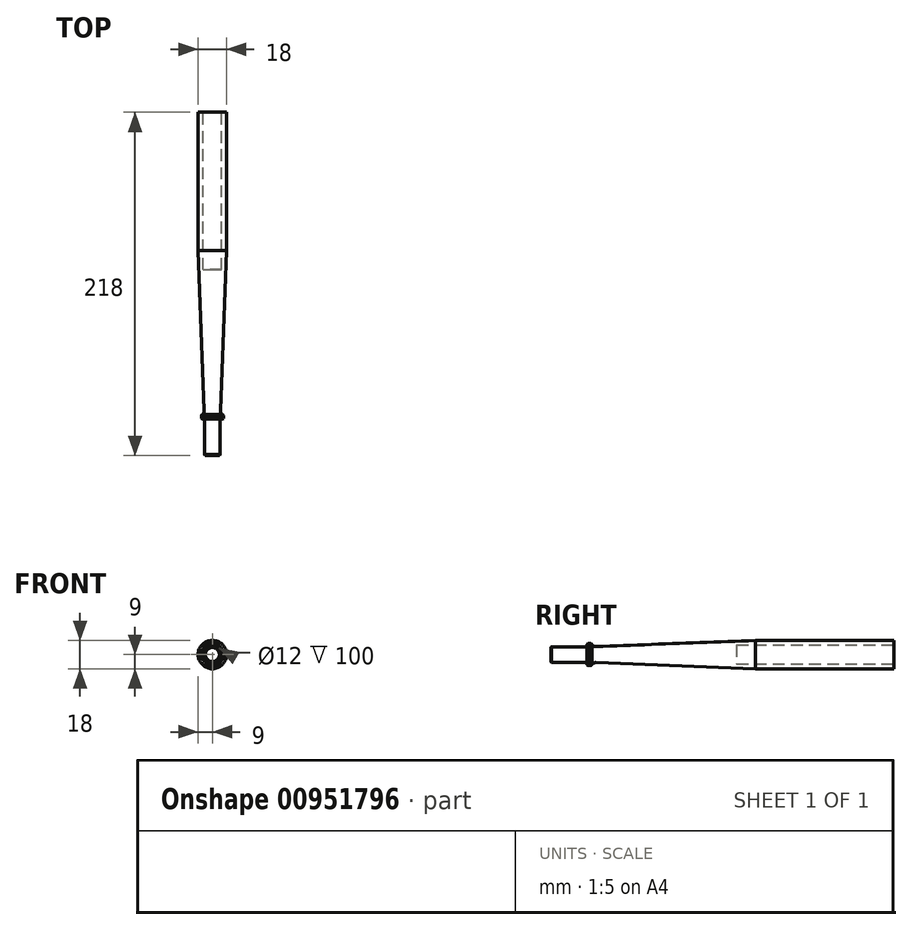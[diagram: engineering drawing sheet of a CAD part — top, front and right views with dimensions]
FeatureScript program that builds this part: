
annotation { "Feature Type Name" : "Feature", "Feature Type Description" : "" }
export const myFeature = defineFeature(function(context is Context, id is Id, definition is map)
    precondition{}
    {
        {
            var Q0;
            Q0=qCreatedBy(makeId("Right.planeOp"),FACE);
            var sketch = newSketch(context, id + "F0", { "sketchPlane" : qUnion([Q0])});
            skLineSegment(sketch, "E0", {"start": v(109, 9) * mm, "end": v(21, 9) * mm});
            skLineSegment(sketch, "E1", {"start": v(109, 9) * mm, "end": v(109, 0) * mm});
            skLineSegment(sketch, "E2", {"start": v(-109, 0) * mm, "end": v(-109, 5) * mm});
            skLineSegment(sketch, "E3", {"start": v(-109, 5) * mm, "end": v(-86, 5) * mm});
            skLineSegment(sketch, "E4", {"start": v(-86, 5) * mm, "end": v(-86, 7) * mm});
            skLineSegment(sketch, "E5", {"start": v(-86, 7) * mm, "end": v(-83, 7) * mm});
            skLineSegment(sketch, "E6", {"start": v(-83, 7) * mm, "end": v(-83, 5) * mm});
            skLineSegment(sketch, "E7", {"start": v(-83, 5) * mm, "end": v(21, 9) * mm});
            skLineSegment(sketch, "E8", {"start": v(109, 0) * mm, "end": v(-109, 0) * mm});
            skSolve(sketch);
        }
        {
            var Q0;
            Q0=makeQuery(id+"F0.imprint","IMPRINT",FACE,{"disambiguationData":[TD([[makeQuery(id+"F0.imprint","IMPRINT",EDGE,{"derivedFrom":sQuery(id+"F0.wireOp",EDGE,"E0")}),1.0]])]});
            var Q1;
            Q1=sQuery(id+"F0.wireOp",EDGE,"E8");
            revolve(context, id + "F1", {"surfaceOperationType" : NewSurfaceOperationType.NEW, "entities" : qUnion([Q0]), "axis" : qUnion([Q1]), "revolveType" : RevolveType.FULL});
        }
        {
            var Q0;
            Q0=makeQuery(id+"F1.opRevolve","SWEPT_FACE",FACE,{"disambiguationData":[OSD([sQuery(id+"F0.wireOp",EDGE,"E1")])]});
            var sketch = newSketch(context, id + "F2", { "sketchPlane" : qUnion([Q0])});
            skCircle(sketch, "E9", {"center": v(0, 0) * mm, "radius": 6 * mm});
            skSolve(sketch);
        }
        {
            var Q0;
            Q0=makeQuery(id+"F2.imprint","IMPRINT",FACE,{"disambiguationData":[TD([[makeQuery(id+"F2.imprint","IMPRINT",EDGE,{"derivedFrom":sQuery(id+"F2.wireOp",EDGE,"E9")}),1.0]])]});
            extrude(context, id + "F3", {"entities" : qUnion([Q0]), "operationType" : NewBodyOperationType.REMOVE, "oppositeDirection" : true, "depth" : 100 * mm, "offsetDistance" : 25 * mm});
        }
        {
            var Q0;
            Q0=makeQuery(id+"F1.opRevolve","SWEPT_EDGE",EDGE,{"disambiguationData":[OSD([sQuery(id+"F0.wireOp",EDGE,"E2"),sQuery(id+"F0.wireOp",EDGE,"E3")])]});
            var Q1;
            Q1=makeQuery(id+"F1.opRevolve","SWEPT_EDGE",EDGE,{"disambiguationData":[OSD([sQuery(id+"F0.wireOp",EDGE,"E5"),sQuery(id+"F0.wireOp",EDGE,"E6")])]});
            var Q2;
            Q2=makeQuery(id+"F1.opRevolve","SWEPT_EDGE",EDGE,{"disambiguationData":[OSD([sQuery(id+"F0.wireOp",EDGE,"E4"),sQuery(id+"F0.wireOp",EDGE,"E5")])]});
            chamfer(context, id + "F4", {"entities" : qUnion([Q0, Q1, Q2]), "width" : 0.5 * mm, "tangentPropagation" : true});
        }
        {
            var Q0;
            Q0=makeQuery(id+"F1.opRevolve","SWEPT_EDGE",EDGE,{"disambiguationData":[OSD([sQuery(id+"F0.wireOp",EDGE,"E6"),sQuery(id+"F0.wireOp",EDGE,"E7")])]});
            fillet(context, id + "F5", {"entities" : qUnion([Q0]), "radius" : 3 * mm, "tangentPropagation" : true, "allowEdgeOverflow" : false});
        }
    });
